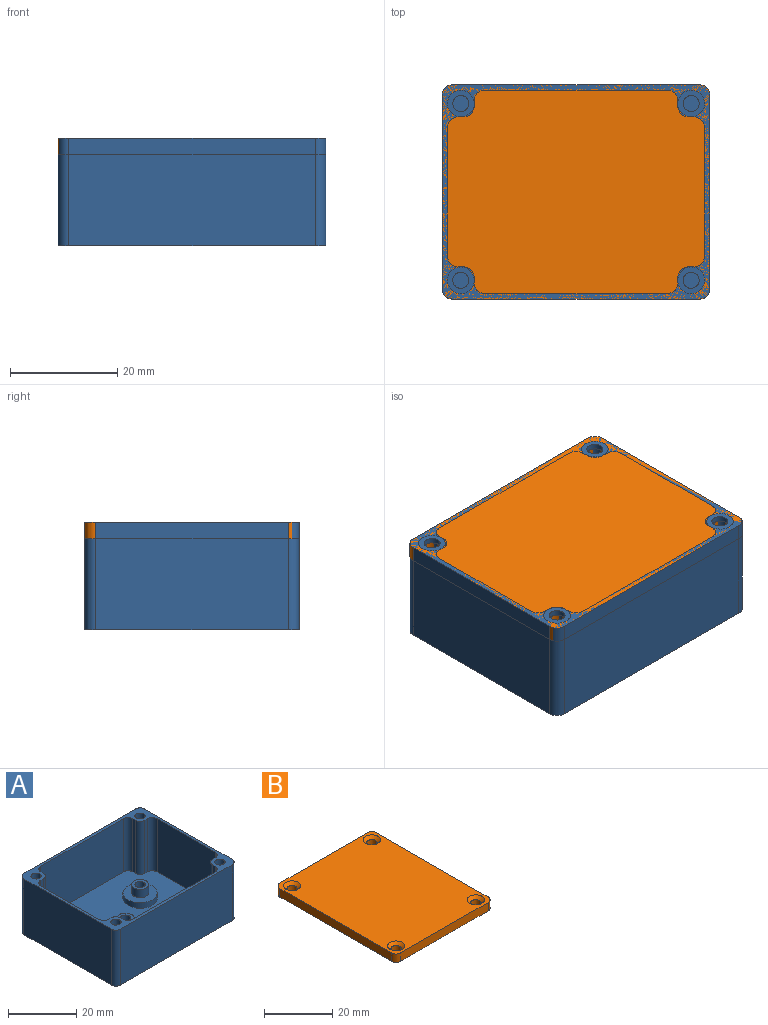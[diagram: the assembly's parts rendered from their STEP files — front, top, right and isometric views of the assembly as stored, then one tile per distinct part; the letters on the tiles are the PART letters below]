
ASSEMBLY  parts=2 mates=1
PART A: 75 faces, bbox 50x40x20 mm
  f0: plane 24x19mm, normal (-1,0,0), area 440.8mm2, adj f4,f8,f53,f62,f63,f64,f65,f66
  f1: plane 36x20mm, normal (1,0,0), area 696mm2, adj f8,f12,f69,f70,f71,f72,f73,f74
  f2: cylinder r=1.5mm len=4mm, axis (0,0,-1), area 37.7mm2, adj f30,f50
  f3: cylinder r=1.5mm len=4mm, axis (0,0,-1), area 37.7mm2, adj f32,f43
  f4: plane 48x38mm, normal (0,0,1), area 1563.5mm2, adj f0,f5,f6,f7,f13,f14,f15,f16
  f5: plane 24x19mm, normal (1,0,0), area 456mm2, adj f4,f8,f56,f57
  f6: plane 34x19mm, normal (0,1,0), area 646mm2, adj f4,f8,f51,f55
  f7: plane 34x19mm, normal (0,-1,0), area 646mm2, adj f4,f8,f59,f61
  f8: plane 50x40mm, normal (0,0,1), area 247.7mm2, adj f0,f1,f5,f6,f7,f9,f10,f11
  f9: plane 46x20mm, normal (0,1,0), area 920mm2, adj f8,f12,f67,f70
  f10: plane 36x20mm, normal (-1,0,0), area 720mm2, adj f8,f12,f67,f68
  f11: plane 46x20mm, normal (0,-1,0), area 920mm2, adj f8,f12,f68,f69
  f12: plane 50x40mm, normal (0,0,-1), area 1949.8mm2, adj f1,f9,f10,f11,f37,f38,f39,f40
  f13: plane 19x1mm, normal (0,-1,0), area 19mm2, adj f4,f8,f60,f62
  f14: plane 19x1mm, normal (-1,0,0), area 19mm2, adj f4,f8,f60,f61
  f15: plane 19x1mm, normal (0,1,0), area 19mm2, adj f4,f8,f54,f56
  f16: plane 19x1mm, normal (1,0,0), area 19mm2, adj f4,f8,f54,f55
  f17: plane 19x1mm, normal (0,1,0), area 19mm2, adj f4,f8,f52,f53
  f18: plane 19x1mm, normal (-1,0,0), area 19mm2, adj f4,f8,f51,f52
  f19: plane 19x1mm, normal (0,-1,0), area 19mm2, adj f4,f8,f57,f58
  f20: plane 19x1mm, normal (1,0,0), area 19mm2, adj f4,f8,f58,f59
  f21: cylinder r=1.5mm len=5mm, axis (0,0,1), area 47.1mm2, adj f8,f22
  f22: plane 3x3mm, normal (0,0,1), area 7.1mm2, adj f21
  f23: cylinder r=1.5mm len=5mm, axis (0,0,1), area 47.1mm2, adj f8,f24
  f24: plane 3x3mm, normal (0,0,1), area 7.1mm2, adj f23
  f25: cylinder r=1.5mm len=5mm, axis (0,0,1), area 47.1mm2, adj f8,f26
  f26: plane 3x3mm, normal (0,0,1), area 7.1mm2, adj f25
  f27: cylinder r=1.5mm len=5mm, axis (0,0,1), area 47.1mm2, adj f8,f28
  f28: plane 3x3mm, normal (0,0,1), area 7.1mm2, adj f27
  f29: cylinder r=2.5mm len=5mm, axis (0,0,-1), area 47.1mm2, adj f30,f34
  f30: plane 5x5mm, normal (0,0,1), area 12.6mm2, adj f2,f29
  f31: cylinder r=2.5mm len=5mm, axis (0,0,-1), area 47.1mm2, adj f32,f36
  f32: plane 5x5mm, normal (0,0,1), area 12.6mm2, adj f3,f31
  f33: cylinder r=5mm len=10mm, axis (0,0,-1), area 62.8mm2, adj f4,f34
  f34: plane 10x10mm, normal (0,0,1), area 58.9mm2, adj f29,f33
  f35: cylinder r=5mm len=10mm, axis (0,0,-1), area 62.8mm2, adj f4,f36
  f36: plane 10x10mm, normal (0,0,1), area 58.9mm2, adj f31,f35
  f37: plane 2.48x2mm, normal (-0.56,-0.83,0), area 6mm2, adj f12,f38,f42,f43
  f38: plane 2.99x2mm, normal (-1,0.07,0), area 6mm2, adj f12,f37,f39,f43
  f39: plane 2.7x2mm, normal (-0.43,0.9,0), area 6mm2, adj f12,f38,f40,f43
  f40: plane 2.48x2mm, normal (0.56,0.83,0), area 6mm2, adj f12,f39,f41,f43
  f41: plane 2.99x2mm, normal (1,-0.07,0), area 6mm2, adj f12,f40,f42,f43
  f42: plane 2.7x2mm, normal (0.43,-0.9,0), area 6mm2, adj f12,f37,f41,f43
  f43: plane 5.98x5.41mm, normal (0,0,-1), area 16.3mm2, adj f3,f37,f38,f39,f40,f41,f42
  f44: plane 2.69x2mm, normal (0.9,-0.44,0), area 6mm2, adj f12,f45,f49,f50
  f45: plane 2.99x2mm, normal (0.07,-1,0), area 6mm2, adj f12,f44,f46,f50
  f46: plane 2.49x2mm, normal (-0.83,-0.56,0), area 6mm2, adj f12,f45,f47,f50
  f47: plane 2.69x2mm, normal (-0.9,0.44,0), area 6mm2, adj f12,f46,f48,f50
  f48: plane 2.99x2mm, normal (-0.07,1,0), area 6mm2, adj f12,f47,f49,f50
  f49: plane 2.49x2mm, normal (0.83,0.56,0), area 6mm2, adj f12,f44,f48,f50
  f50: plane 5.99x5.39mm, normal (0,0,-1), area 16.3mm2, adj f2,f44,f45,f46,f47,f48,f49
  f51: cylinder r=2mm len=19mm, axis (0,0,1), area 59.7mm2, adj f4,f6,f8,f18
  f52: cylinder r=2mm len=19mm, axis (0,0,1), area 59.7mm2, adj f4,f8,f17,f18
  f53: cylinder r=2mm len=19mm, axis (0,0,-1), area 59.7mm2, adj f0,f4,f8,f17
  f54: cylinder r=2mm len=19mm, axis (0,0,1), area 59.7mm2, adj f4,f8,f15,f16
  f55: cylinder r=2mm len=19mm, axis (0,0,-1), area 59.7mm2, adj f4,f6,f8,f16
  f56: cylinder r=2mm len=19mm, axis (0,0,-1), area 59.7mm2, adj f4,f5,f8,f15
  f57: cylinder r=2mm len=19mm, axis (0,0,1), area 59.7mm2, adj f4,f5,f8,f19
  f58: cylinder r=2mm len=19mm, axis (0,0,1), area 59.7mm2, adj f4,f8,f19,f20
  f59: cylinder r=2mm len=19mm, axis (0,0,-1), area 59.7mm2, adj f4,f7,f8,f20
  f60: cylinder r=2mm len=19mm, axis (0,0,1), area 59.7mm2, adj f4,f8,f13,f14
  f61: cylinder r=2mm len=19mm, axis (0,0,1), area 59.7mm2, adj f4,f7,f8,f14
  f62: cylinder r=2mm len=19mm, axis (0,0,1), area 59.7mm2, adj f0,f4,f8,f13
  f63: plane 4.07x0.5mm, normal (0,0,-1), area 2mm2, adj f0,f64,f66,f74
  f64: plane 3.74x0.5mm, normal (0,1,0), area 1.9mm2, adj f0,f63,f65,f72
  f65: plane 4.07x0.5mm, normal (0,0,1), area 2mm2, adj f0,f64,f66,f71
  f66: plane 3.74x0.5mm, normal (0,-1,0), area 1.9mm2, adj f0,f63,f65,f73
  f67: cylinder r=2mm len=20mm, axis (0,0,1), area 62.8mm2, adj f8,f9,f10,f12
  f68: cylinder r=2mm len=20mm, axis (0,0,-1), area 62.8mm2, adj f8,f10,f11,f12
  f69: cylinder r=2mm len=20mm, axis (0,0,1), area 62.8mm2, adj f1,f8,f11,f12
  f70: cylinder r=2mm len=20mm, axis (0,0,-1), area 62.8mm2, adj f1,f8,f9,f12
  f71: plane 5.07x0.5mm, normal (0.71,0,0.71), area 3.2mm2, adj f1,f65,f72,f73
  f72: plane 4.74x0.5mm, normal (0.71,0.71,0), area 3mm2, adj f1,f64,f71,f74
  f73: plane 4.74x0.5mm, normal (0.71,-0.71,0), area 3mm2, adj f1,f66,f71,f74
  f74: plane 5.07x0.5mm, normal (0.71,0,-0.71), area 3.2mm2, adj f1,f63,f72,f73
PART B: 18 faces, bbox 40x50x3 mm
  f0: plane 36x3mm, normal (0,1,0), area 108mm2, adj f8,f9,f14,f17
  f1: plane 46x3mm, normal (-1,0,0), area 138mm2, adj f8,f9,f14,f15
  f2: plane 36x3mm, normal (0,-1,0), area 108mm2, adj f8,f9,f15,f16
  f3: cylinder r=1.5mm len=3mm, axis (0,0,-1), area 18.8mm2, adj f9,f13
  f4: cylinder r=1.5mm len=3mm, axis (0,0,-1), area 18.8mm2, adj f9,f12
  f5: cylinder r=1.5mm len=3mm, axis (0,0,-1), area 18.8mm2, adj f9,f10
  f6: cylinder r=1.5mm len=3mm, axis (0,0,-1), area 18.8mm2, adj f9,f11
  f7: plane 46x3mm, normal (1,0,0), area 138mm2, adj f8,f9,f16,f17
  f8: plane 50x40mm, normal (0,0,1), area 1918mm2, adj f0,f1,f2,f7,f10,f11,f12,f13
  f9: plane 50x40mm, normal (0,0,-1), area 1968.3mm2, adj f0,f1,f2,f3,f4,f5,f6,f7
  f10: cone r=1.5mm half-angle=45deg, axis (0,0,1), area 17.8mm2, adj f5,f8
  f11: cone r=1.5mm half-angle=45deg, axis (0,0,1), area 17.8mm2, adj f6,f8
  f12: cone r=1.5mm half-angle=45deg, axis (0,0,1), area 17.8mm2, adj f4,f8
  f13: cone r=1.5mm half-angle=45deg, axis (0,0,1), area 17.8mm2, adj f3,f8
  f14: cylinder r=2mm len=3mm, axis (0,0,1), area 9.4mm2, adj f0,f1,f8,f9
  f15: cylinder r=2mm len=3mm, axis (0,0,-1), area 9.4mm2, adj f1,f2,f8,f9
  f16: cylinder r=2mm len=3mm, axis (0,0,1), area 9.4mm2, adj f2,f7,f8,f9
  f17: cylinder r=2mm len=3mm, axis (0,0,-1), area 9.4mm2, adj f0,f7,f8,f9
PLACE A t=(-13.63,12.46,20.67)mm fixed
PLACE B rot(axis=(0,0,1),90deg) t=(-72.24,76.93,37.67)mm
MATE slider A.f23 <-> B.f4  axis (0,0,1) through (-70.2,62.26,40.67)mm
